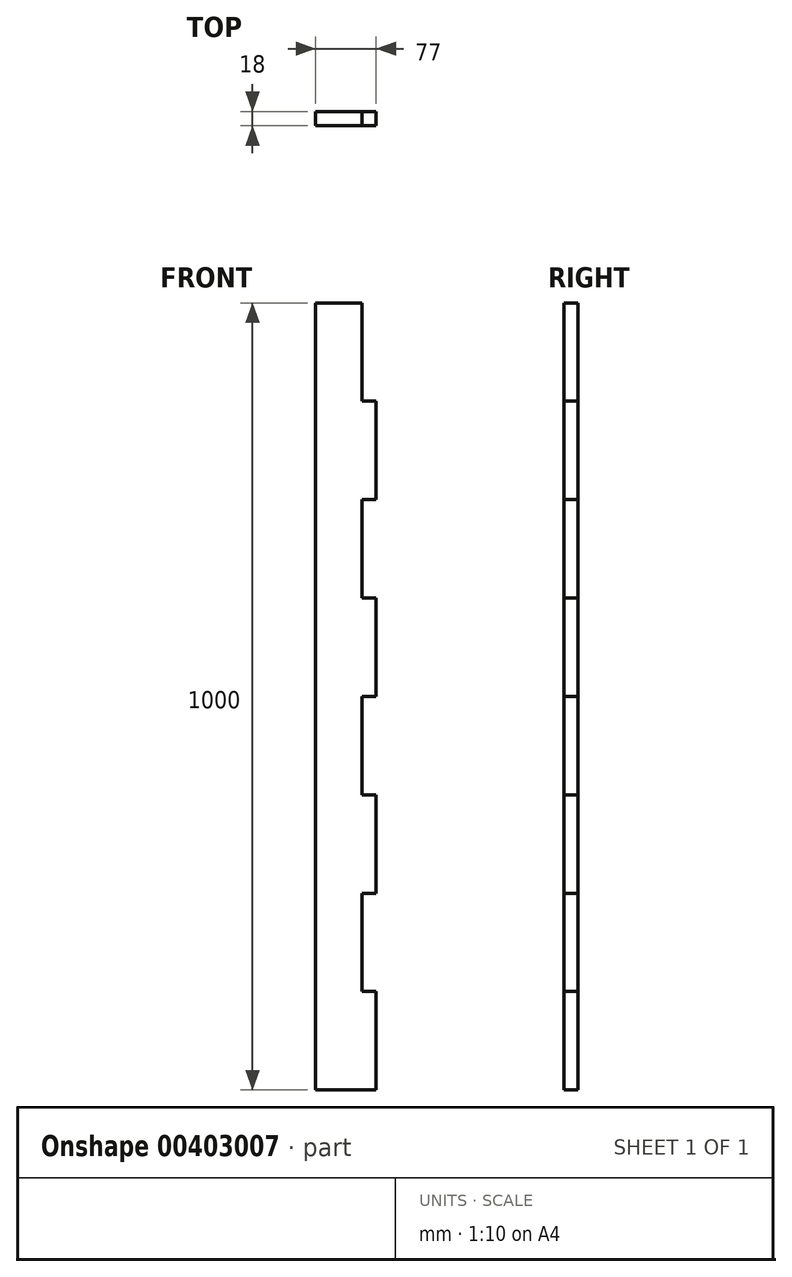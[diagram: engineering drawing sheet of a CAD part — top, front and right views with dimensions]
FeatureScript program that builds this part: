
annotation { "Feature Type Name" : "Feature", "Feature Type Description" : "" }
export const myFeature = defineFeature(function(context is Context, id is Id, definition is map)
    precondition{}
    {
        {
            var Q0;
            Q0=qCreatedBy(makeId("Front.planeOp"),FACE);
            var sketch = newSketch(context, id + "F0", { "sketchPlane" : qUnion([Q0])});
            skLineSegment(sketch, "E0.bottom", {"start": v(0, 0) * mm, "end": v(77, 0) * mm});
            skLineSegment(sketch, "E0.top", {"start": v(0, 1000) * mm, "end": v(59, 1000) * mm});
            skLineSegment(sketch, "E0.left", {"start": v(0, 0) * mm, "end": v(0, 1000) * mm});
            skLineSegment(sketch, "E0.right", {"start": v(77, 0) * mm, "end": v(77, 125) * mm});
            skLineSegment(sketch, "E1.top", {"start": v(77, 875) * mm, "end": v(59, 875) * mm});
            skLineSegment(sketch, "E1.right", {"start": v(59, 1000) * mm, "end": v(59, 875) * mm});
            skLineSegment(sketch, "E2.bottom", {"start": v(77, 750) * mm, "end": v(59, 750) * mm});
            skLineSegment(sketch, "E2.top", {"start": v(77, 625) * mm, "end": v(59, 625) * mm});
            skLineSegment(sketch, "E2.right", {"start": v(59, 750) * mm, "end": v(59, 625) * mm});
            skLineSegment(sketch, "E3.bottom", {"start": v(77, 500) * mm, "end": v(59, 500) * mm});
            skLineSegment(sketch, "E3.top", {"start": v(77, 375) * mm, "end": v(59, 375) * mm});
            skLineSegment(sketch, "E3.right", {"start": v(59, 500) * mm, "end": v(59, 375) * mm});
            skLineSegment(sketch, "E4.bottom", {"start": v(77, 250) * mm, "end": v(59, 250) * mm});
            skLineSegment(sketch, "E4.top", {"start": v(77, 125) * mm, "end": v(59, 125) * mm});
            skLineSegment(sketch, "E4.right", {"start": v(59, 250) * mm, "end": v(59, 125) * mm});
            skLineSegment(sketch, "E5.trimOffspring", {"start": v(77, 750) * mm, "end": v(77, 875) * mm});
            skLineSegment(sketch, "E6.trimOffspring", {"start": v(77, 500) * mm, "end": v(77, 625) * mm});
            skLineSegment(sketch, "E7.trimOffspring", {"start": v(77, 250) * mm, "end": v(77, 375) * mm});
            skSolve(sketch);
        }
        {
            var Q0;
            Q0=makeQuery(id+"F0.imprint","IMPRINT",FACE,{"disambiguationData":[TD([[makeQuery(id+"F0.imprint","IMPRINT",EDGE,{"derivedFrom":sQuery(id+"F0.wireOp",EDGE,"kHmZVxOG-gPJc-REYJ-O9rl-HYASeAGw87Q2.bottom")}),1.0]])]});
            var Q1;
            Q1=makeQuery(id+"F0.imprint","IMPRINT",FACE,{"disambiguationData":[TD([[makeQuery(id+"F0.imprint","IMPRINT",EDGE,{"derivedFrom":sQuery(id+"F0.wireOp",EDGE,"E0.bottom")}),1.0]])]});
            extrude(context, id + "F1", {"entities" : qUnion([Q0, Q1]), "depth" : 18 * mm});
        }
    });
